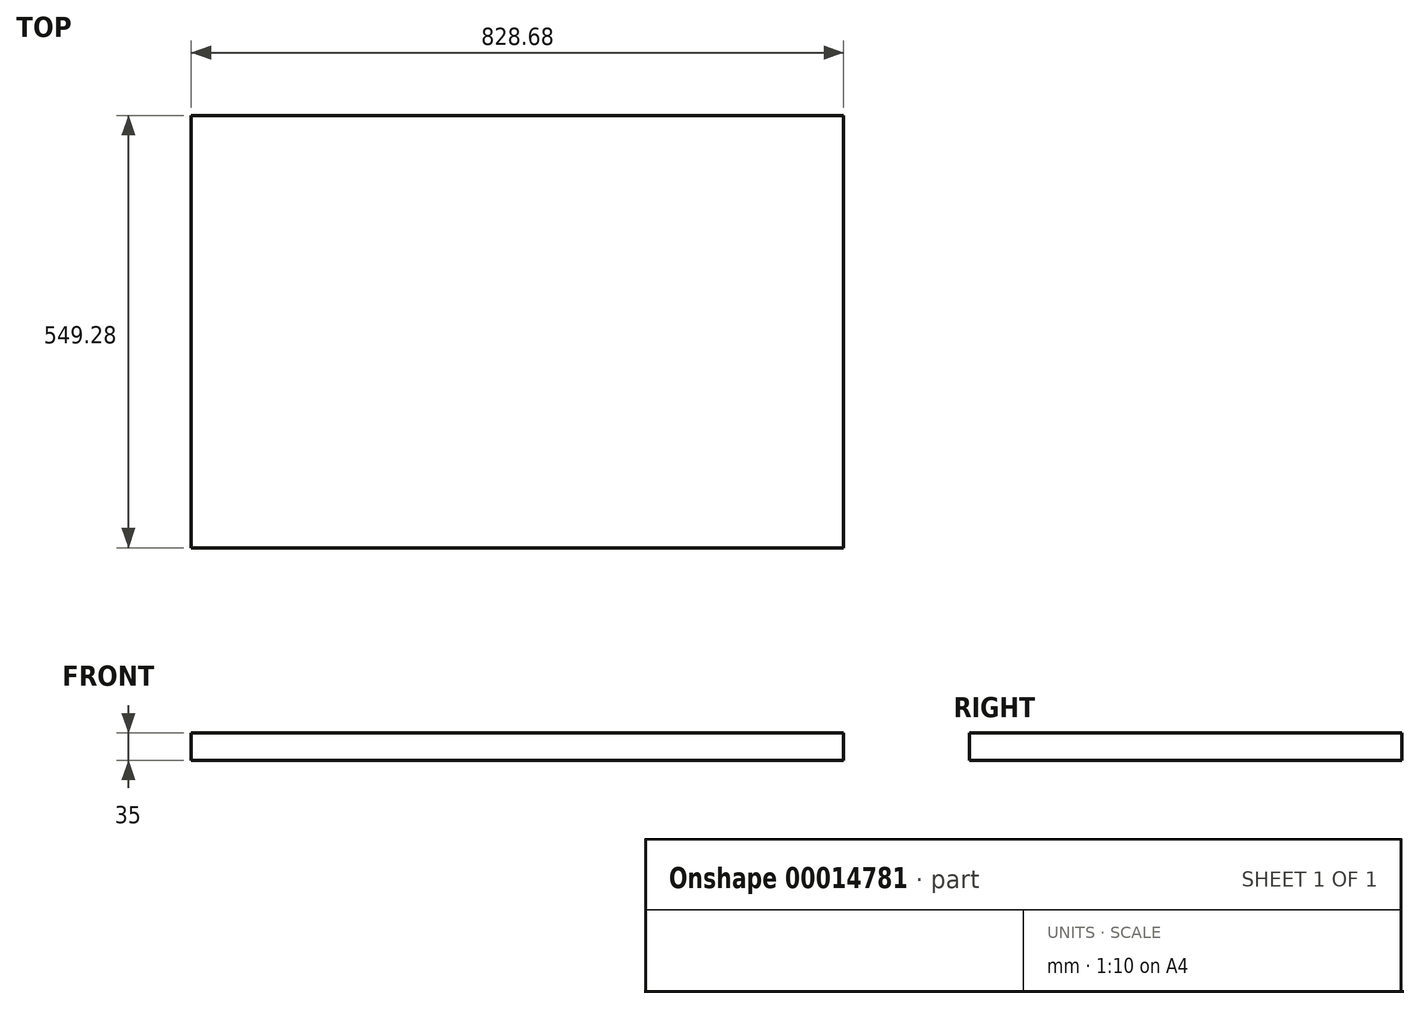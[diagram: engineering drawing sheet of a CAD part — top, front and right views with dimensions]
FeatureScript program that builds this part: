
annotation { "Feature Type Name" : "Feature", "Feature Type Description" : "" }
export const myFeature = defineFeature(function(context is Context, id is Id, definition is map)
    precondition{}
    {
        {
            var Q0;
            Q0=qCreatedBy(makeId("Top.planeOp"),FACE);
            var sketch = newSketch(context, id + "F0", { "sketchPlane" : qUnion([Q0])});
            skLineSegment(sketch, "E0.rect.bottom", {"start": v(414.34, -274.64) * mm, "end": v(-414.34, -274.64) * mm});
            skLineSegment(sketch, "E0.rect.top", {"start": v(414.34, 274.64) * mm, "end": v(-414.34, 274.64) * mm});
            skLineSegment(sketch, "E0.rect.left", {"start": v(414.34, -274.64) * mm, "end": v(414.34, 274.64) * mm});
            skLineSegment(sketch, "E0.rect.right", {"start": v(-414.34, -274.64) * mm, "end": v(-414.34, 274.64) * mm});
            skPoint(sketch, "E0.rect.middle", {"position": v(0, 0) * mm});
            skSolve(sketch);
        }
        {
            var Q0;
            Q0 = qSketchRegion(id + "F0", true);
            extrude(context, id + "F1", {"entities" : qUnion([Q0]), "depth" : 35 * mm});
        }
    });
